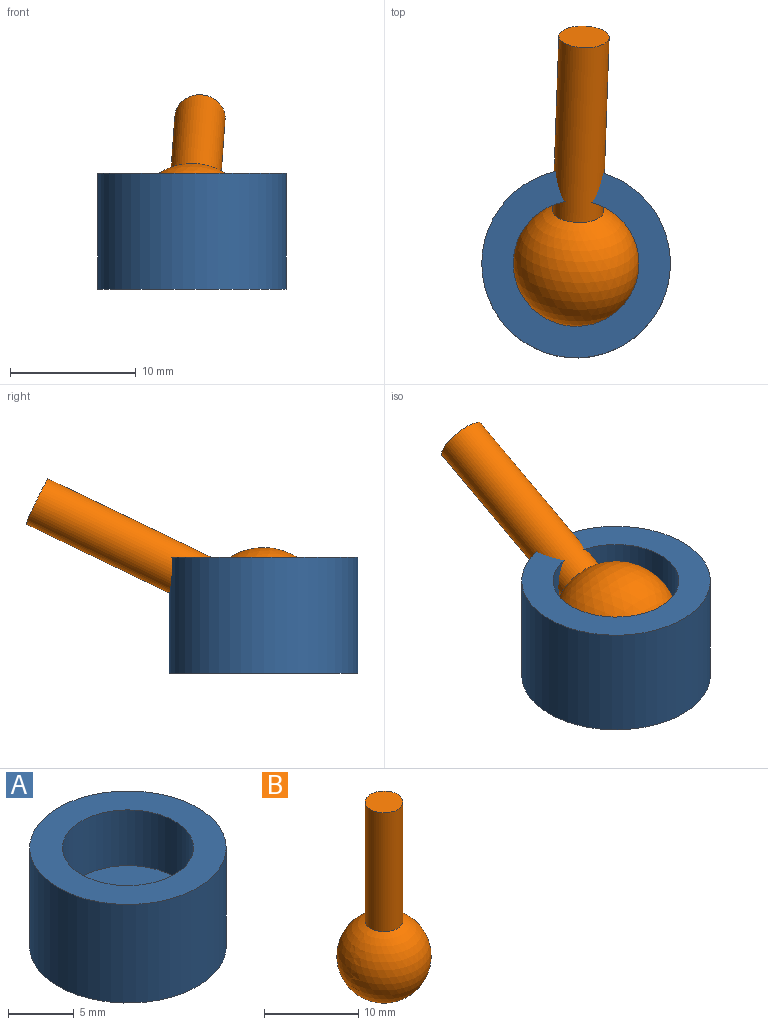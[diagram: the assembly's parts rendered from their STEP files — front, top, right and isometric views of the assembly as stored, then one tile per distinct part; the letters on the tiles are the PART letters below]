
ASSEMBLY  parts=2 mates=1
PART A: 5 faces, bbox 15x15x9.2 mm
  f0: plane 15x15mm, normal (0,0,-1), area 176.7mm2, adj f1
  f1: cylinder r=7.5mm len=15mm, axis (0,0,-1), area 434mm2, adj f0,f2
  f2: plane 15x15mm, normal (0,0,1), area 98.2mm2, adj f1,f3
  f3: cylinder r=5mm len=10mm, axis (0,0,-1), area 163.6mm2, adj f2,f4
  f4: plane 10x10mm, normal (0,0,1), area 78.5mm2, adj f3
PART B: 3 faces, bbox 10x10x25 mm
  f0: sphere r=5mm, area 301mm2, adj f1
  f1: cylinder r=2mm len=15.42mm, axis (0,0,-1), area 193.7mm2, adj f0,f2
  f2: plane 4x4mm, normal (0,0,1), area 12.6mm2, adj f1
PLACE A t=(-2.36,-1.8,8.66)mm fixed
PLACE B rot(axis=(-0.98,-0.08,-0.19),65.6deg) t=(-3.02,-20.67,4.58)mm
MATE ball B.f1 <-> A.f1  axis (0.03,0.9,0.43) through (-2.36,-1.8,13.66)mm
